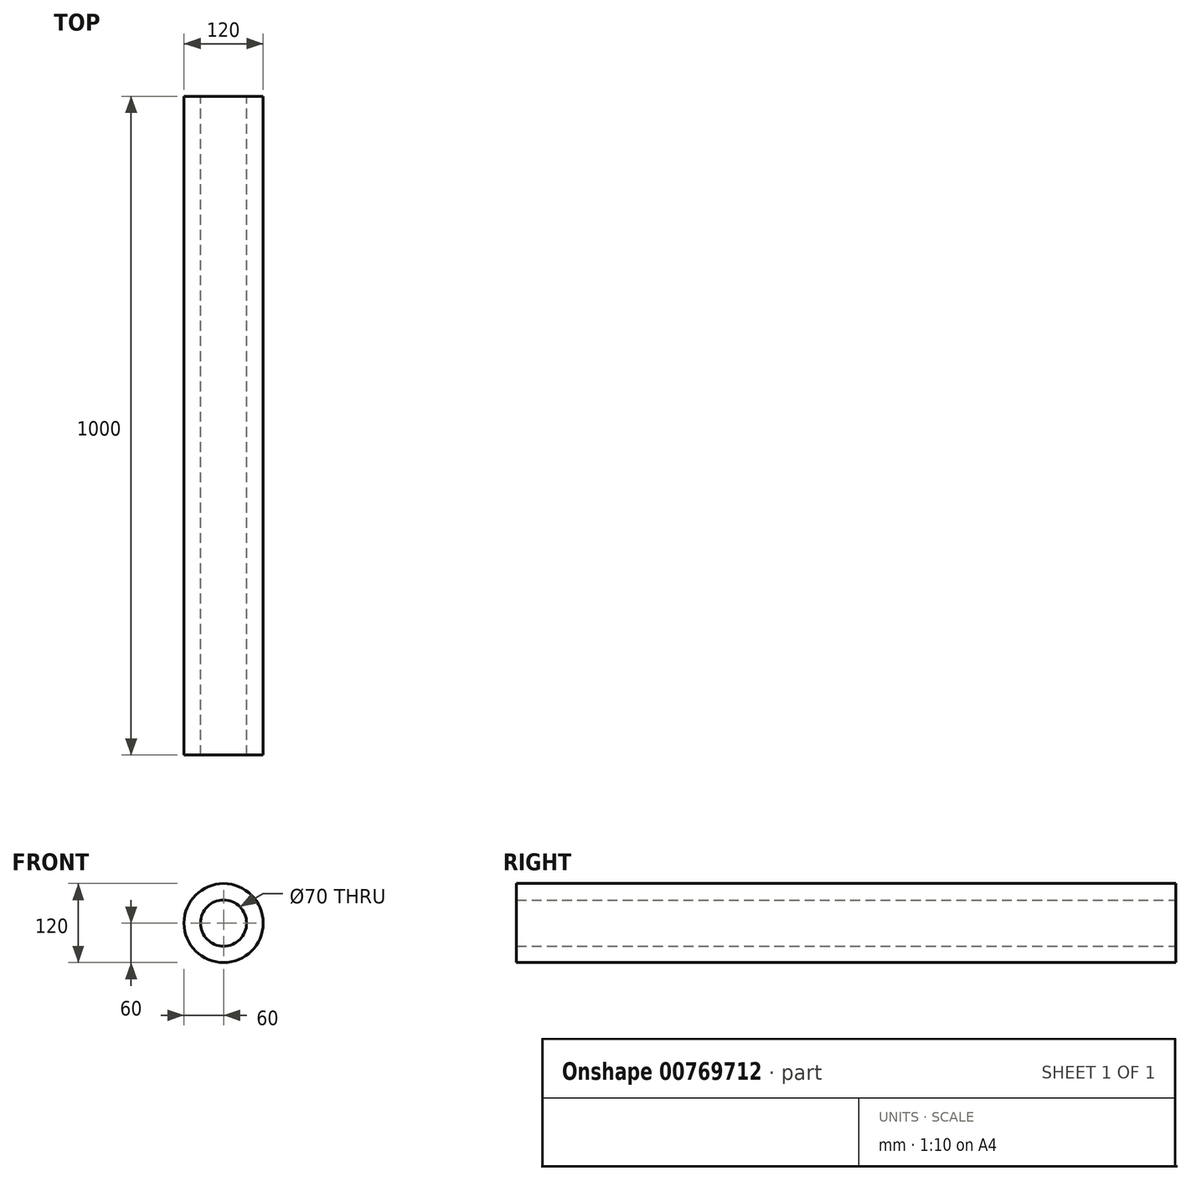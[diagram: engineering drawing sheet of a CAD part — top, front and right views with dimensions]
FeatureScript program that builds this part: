
annotation { "Feature Type Name" : "Feature", "Feature Type Description" : "" }
export const myFeature = defineFeature(function(context is Context, id is Id, definition is map)
    precondition{}
    {
        {
            var Q0;
            Q0=qCreatedBy(makeId("Front.planeOp"),FACE);
            var sketch = newSketch(context, id + "F0", { "sketchPlane" : qUnion([Q0])});
            skCircle(sketch, "E0", {"center": v(0, 0) * mm, "radius": 35 * mm});
            skCircle(sketch, "E1", {"center": v(0, 0) * mm, "radius": 60 * mm});
            skSolve(sketch);
        }
        {
            var Q0;
            Q0 = qSketchRegion(id + "F0", true);
            extrude(context, id + "F1", {"entities" : qUnion([Q0]), "depth" : 1000 * mm, "offsetDistance" : 25 * mm});
        }
        {
            var Q0;
            Q0=qCreatedBy(makeId("Top.planeOp"),FACE);
            var Q1;
            Q1 = qBodyType(qCreatedBy(id + "FUtsWJixU4UP7hT_1" ,EDGE), BodyType.WIRE);
            cPlane(context, id + "F2", {"entities" : qUnion([Q0, Q1]), "cplaneType" : CPlaneType.OFFSET, "offset" : 35 * mm, "width" : 150 * mm, "height" : 150 * mm});
        }
        {
            var Q0;
            Q0=qCreatedBy(id+"F2.planeOp",FACE);
            var sketch = newSketch(context, id + "F3", { "sketchPlane" : qUnion([Q0])});
            skPoint(sketch, "E2", {"position": v(0, -15) * mm});
            skCircle(sketch, "E3", {"center": v(0, -15) * mm, "radius": 15 * mm});
            skSolve(sketch);
        }
        {
            var Q0;
            Q0=sQuery(id+"F3.wireOp",EDGE,"E3");
            extrude(context, id + "F4", {"bodyType" : ToolBodyType.SURFACE, "surfaceEntities" : qUnion([Q0]), "depth" : 125 * mm, "offsetDistance" : 25 * mm});
        }
        {
            var Q0;
            Q0=qCreatedBy(makeId("Top.planeOp"),FACE);
            cPlane(context, id + "F5", {"entities" : qUnion([Q0]), "cplaneType" : CPlaneType.OFFSET, "offset" : 35 * mm, "oppositeDirection" : true, "width" : 150 * mm, "height" : 150 * mm});
        }
        {
            var Q0;
            Q0=makeQuery(id+"F4.opExtrude","SWEPT_BODY",BODY,{"disambiguationData":[OSD([sQuery(id+"F3.wireOp",EDGE,"E3")])]});
            var Q1;
            Q1=qCreatedBy(makeId("Top.planeOp"),FACE);
            mirror(context, id + "F6", {"entities" : qUnion([Q0]), "mirrorPlane" : qUnion([Q1])});
        }
        {
            var Q0;
            Q0=qCreatedBy(makeId("Front.planeOp"),FACE);
            cPlane(context, id + "F7", {"entities" : qUnion([Q0]), "cplaneType" : CPlaneType.OFFSET, "offset" : 500 * mm, "width" : 150 * mm, "height" : 150 * mm});
        }
        {
            var Q0;
            Q0=makeQuery(id+"F6.opPattern","COPY",BODY,{"derivedFrom":makeQuery(id+"F4.opExtrude","SWEPT_BODY",BODY,{"disambiguationData":[OSD([sQuery(id+"F3.wireOp",EDGE,"E3")])]}),"instanceName":"1"});
            var Q1;
            Q1=qCreatedBy(id+"F7.planeOp",FACE);
            mirror(context, id + "F8", {"entities" : qUnion([Q0]), "mirrorPlane" : qUnion([Q1])});
        }
    });
